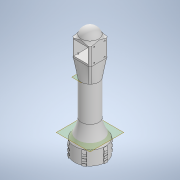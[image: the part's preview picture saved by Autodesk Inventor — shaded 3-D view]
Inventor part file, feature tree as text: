
AUTODESK INVENTOR PART (.ipt)
format: ipt  version: 2022.3 (Build 263350000, 350)  size: 578,048 bytes
history: native  units: mm
features: sketch x16, extrude x10, revolve x3, hole x3, plane x2, fillet x2, loft x1, pattern_circular x1, other x1, projected_geometry x1
ambient origin geometry x8: Origin, YZ Plane, XZ Plane, XY Plane, X Axis, Y Axis, Z Axis, Center Point
bodies: Solid1 (feature_tree)
feature tree (40):
  extrude  "Extrusion1"  Depth=4.0mm
  revolve  "Revolution1"  [1 undecoded]
  plane  "Work Plane1"
  extrude  "Extrusion2"  Depth=100.0mm
  extrude  "Extrusion3"  Depth=25.0mm
  plane  "Work Plane2"
  sketch  "Sketch5"  dims[d12=100.0mm d13=90.0deg]
  fillet  "Fillet1"  Radius=4.0mm
  loft  "Loft1"
  extrude  "Extrusion4"  Depth=5.0mm
  sketch  "Sketch11"  dims[d16=65.0mm d17=65.0mm]
  extrude  "Extrusion7"  Depth=65.0mm
  extrude  "Extrusion8"  Depth=5.0mm
  extrude  "Extrusion9"  Depth=5.0mm TaperAngle=0.0deg
  hole  "Hole2"  [1 undecoded]
  extrude  "Extrusion10"  Depth=5.0mm
  revolve  "Revolution2"  Angle=90.0deg
  fillet  "Fillet3"  [1 undecoded]
  hole  "Hole3"  [1 undecoded]
  hole  "Hole4"  [1 undecoded]
  extrude  "Extrusion11"  Depth=45.0mm
  extrude  "Extrusion12"  Depth=42.0mm TaperAngle=0.0deg
  pattern_circular  "Circular Pattern1"  [2 undecoded]
  revolve  "Revolution3"  [1 undecoded]
  sketch  "Sketch1"  dims[d0=80.0mm d1=4.0mm]
  sketch  "Sketch2"  dims[d2=40.0mm d3=0.0mm d4=88.0mm]
  sketch  "Sketch3"  dims[d5=50.0mm d8=100.0mm]
  sketch  "Sketch4"  dims[d9=25.0mm d10=150.0mm d11=4.0mm]
  other  "Edges1"
  sketch  "Sketch7"  dims[d14=-52.5mm d15=5.0mm]
  projected_geometry  "Projected Loop2"
  sketch  "Sketch12"  dims[d18=5.0mm d19=15.0mm]
  sketch  "Sketch13"  dims[d20=10.0mm d21=5.0mm d22=0.0mm]
  sketch  "Sketch14"  dims[d23=52.0mm d24=52.0mm]
  sketch  "Sketch15"  dims[d25=5.0mm d26=0.0mm d27=50.0mm]
  sketch  "Sketch16"  dims[d28=5.0mm d29=0.0mm d30=90.0deg d31=0.0mm d32=90.0deg]
  sketch  "Sketch17"  dims[d33=100.0mm d34=0.0mm d54=5.0mm]
  sketch  "Sketch18"  dims[d55=4.5mm d56=5.0mm d57=0.0mm]
  sketch  "Sketch19"  dims[d58=45.0mm d59=0.0mm d60=45.0mm]
  sketch  "Sketch20"  dims[d61=22.0mm d62=42.0mm d63=0.0mm d64=31.0mm d65=31.0mm d66=2.4mm d67=6.0mm d68=4.0mm d69=2.0mm d70=90.0deg d71=4.2mm d72=0.0mm d73=3.0mm d74=0.0mm d75=26.0mm d76=26.0mm d77=90.0deg d78=10.0mm d79=0.0mm d80=5.0mm d81=5.0mm d82=5.0mm d83=5.068mm d84=3.4mm d85=6.0mm d86=4.1mm d87=5.1mm d88=90.0deg d89=2.2mm d90=0.0mm d91=5.0mm d92=5.0mm d93=5.0mm d94=5.068mm d95=3.4mm d96=6.0mm d97=4.1mm d98=5.1mm d99=90.0deg d100=2.2mm d101=0.0mm d102=30.0mm d103=40.0mm d104=30.0mm d105=40.0mm d106=4.0mm d107=10.0mm d108=30.0mm d109=0.0mm d110=10.0mm d111=30.0mm d112=0.0mm d113=1.0mm d114=6.0mm d115=1.0mm d116=6.0mm d117=1.0mm d118=6.0mm d119=1.0mm d120=6.0mm d121=1.0mm d122=6.0mm d123=10.0mm d124=90.0deg d125=1.0mm d126=1.0mm d127=90.0deg d128=60.0mm d129=360.0deg]
note: 8 required parameter values undecoded (feature->parameter linkage not recoverable at this tier; creation-order binding heuristic only, values carry confidence <= 0.55)